# Revit family: Remeha_Gas110Eco-65_LOD-5
name_source: partatom
category: Mechanical Equipment
revit_build: Autodesk Revit 2015 (Build: 20160512_1515(x64)
units: mm (PartAtom-declared; Revit-internal decimal feet)

## types (1)
- Gas 110 Eco - 65
    6 Monthly = 0
    Access Clearance Bottom = 0.000 mm
    Access Clearance Front = 700.000 mm
    Access Clearance Left = 25.000 mm
    Access Clearance Rear = 0.000 mm
    Access Clearance Right = 25.000 mm
    Access Clearance Top = 400.000 mm
    Additional Technical Details = https://www.remeha.co.uk
    Air Inlet Connection Size = 150.000 mm
    Annually = As per attached URL O&M manual
    Assembly Code = D3020100
    BMS Links = Yes
    Bespoke Timeframe = 0
    Building Regulations Seasonal Efficiency = 96.30 %
    Burner Control Type = Modulating
    CE Mark = CE - 0063BS3826
    Colour = Remeha White + RAL 2002
    Condensate Drain Size = 32.000 mm
    Condensate Drain Type = Plain
    Configuration = Single boiler
    Control Type = 0 - 10V, Open Therm, Volt free enable, Direct boiler weather compensating control systems available from Remeha as optional extra's.
    Daily = 0
    Default Elevation = 0.000 mm
    Description = Condensing Boiler
    Drain Connection Size = 0.000 mm
    Drain Connection Type = Unset
    Embodied Carbon = 0
    Energy Technology List = https://etl.beis.gov.uk
    Environmental Product Declaration = 0
    ErP Energy Label = A
    ErP Rated Efficiency at Full Load = 88.6 %
    ErP Rated Efficiency at Part Load = 98.1 %
    ErP Seasonal Efficiency = 93 %
    Expected Life = 15
    External Material = Steel
    Features = Remeha's Gas110 range are compact high efficiency floor standing condensing boilers have been developed specifically to fit directly into the floor space as a traditional boiler.
    Finish = Painted
    Flow and Return Connection Size = 32.000 mm
    Flow and Return Connection Type = Threaded
    Flue Connection size = 100.000 mm
    Flue or Air Intake Classification = B23p,C13,C33,C43,C53,C63,C83,C93
    Frequency = 50 Hz
    Fuel Connection Size = 20.000 mm
    Fuel Connection Type = Threaded
    Full Load Current = 0 A
    Fuse Rating = 6 A
    Gas Consumption rate = 6.56 m3/h
    Green Guide for Specification = 0
    Gross Weight = 122.50 kg
    Heat Exchanger Material = Aluminium
    Heater Operation = Condensing
    Hydraulic Resistance at 11C temperature differential = 0.58
    Hydraulic Resistance at 20C temperature differential = 0.18
    IK Rating = 0
    IP Rating = IP21
    IfcExportAs = IfcBoilerType
    IfcExportType = NOTDEFINED
    Interlocks = Yes
    Keynote = Flue Connection size can vary between 100/150 concentric.
    Life Cycle Analysis = 0
    Location of Manufacturer = 0
    Maintenance Required 0 to 300hrs = 0
    Maintenance Required 1001 to 2000hrs = 0
    Maintenance Required 2001 to 4000hrs = 0
    Maintenance Required 301 to 600hrs = 0
    Maintenance Required 4001 to 8000hrs = 0
    Maintenance Required 601 to 1000hrs = 0
    Maintenance Required 8001 to 12000hrs = 0
    Manufacturer = Remeha Commercial
    Manufacturer Website = http://www.remeha.co.uk
    Material Ingredient Reporting = 0
    Maximum Gas Inlet Pressure = 0.03 bar
    Maximum Oil Inlet Pressure = 0.00 bar
    Maximum Operating Pressure = 4.00 bar
    Maximum Power Consumption = 88 W
    Minimum Flow Rate at 11C temperature differential = 1 L/s
    Minimum Flow Rate at 20C temperature differential = 1 L/s
    Minimum Gas Inlet Pressure = 0.02 bar
    Minimum Oil Inlet Pressure = 0.00 bar
    Minimum Operating Pressure = 0.80 bar
    Minimum Power Consumption = 31 W
    Model = Gas 110 Eco - 65
    Monthly = 0
    Mounting = Floor Standing
    NOx Emissions = 32 mg/kWh
    Nominal Gas Inlet Pressure = 0.02 bar
    Nominal Oil Inlet Pressure = 0.00 bar
    Oil Consumption rate = 0
    Operation and Maintenance Manual = https://www.remeha.co.uk
    Optional Fuel = Gas - LPG
    Overall Height = 1100.000 mm
    Overall Length = 663.000 mm
    Overall Width = 600.000 mm
    Primary Fuel = Gas - NG
    Product Literature = https://www.remeha.co.uk
    Product Model Number = 100010820
    Product Range = Gas 110 Eco - 65
    Quarterly = 0
    Rated Criteria = 80/60
    Rated Output = 61000 W
    Reference Standard = 92/42/EEC, 2006/95/EEC, 2004/108/EEC, 97/23/EEC (article 3 sub 3)
    Responsible Extraction of Materials = 0
    Responsible Sourcing of Materials = 0
    Safety Valve Connection Size = 0.000 mm
    Safety Valve Connection Type = Unset
    Shape = Rectangular (Vertical)
    Shipping Weight = 116.00 kg
    Sound Pressure Level = 49 dBA
    Starting Current = 0 A
    Supply Phase = 1
    Turndown Ratio = 5:1
    Type = Space heating
    Voltage = 230 V
    Water Content = 6.5 L
    Water Treatment Required = Yes
    Weekly = 0

note: source unit labels omitted for Hydraulic Resistance at 11C temperature differential, Hydraulic Resistance at 20C temperature differential — the stored unit's dimension contradicts the parameter name (converter mislabeling)

## geometry (parser evidence)
native form markers: Blend x25, Sweep x14
no freeform markers — native parametric forms only
